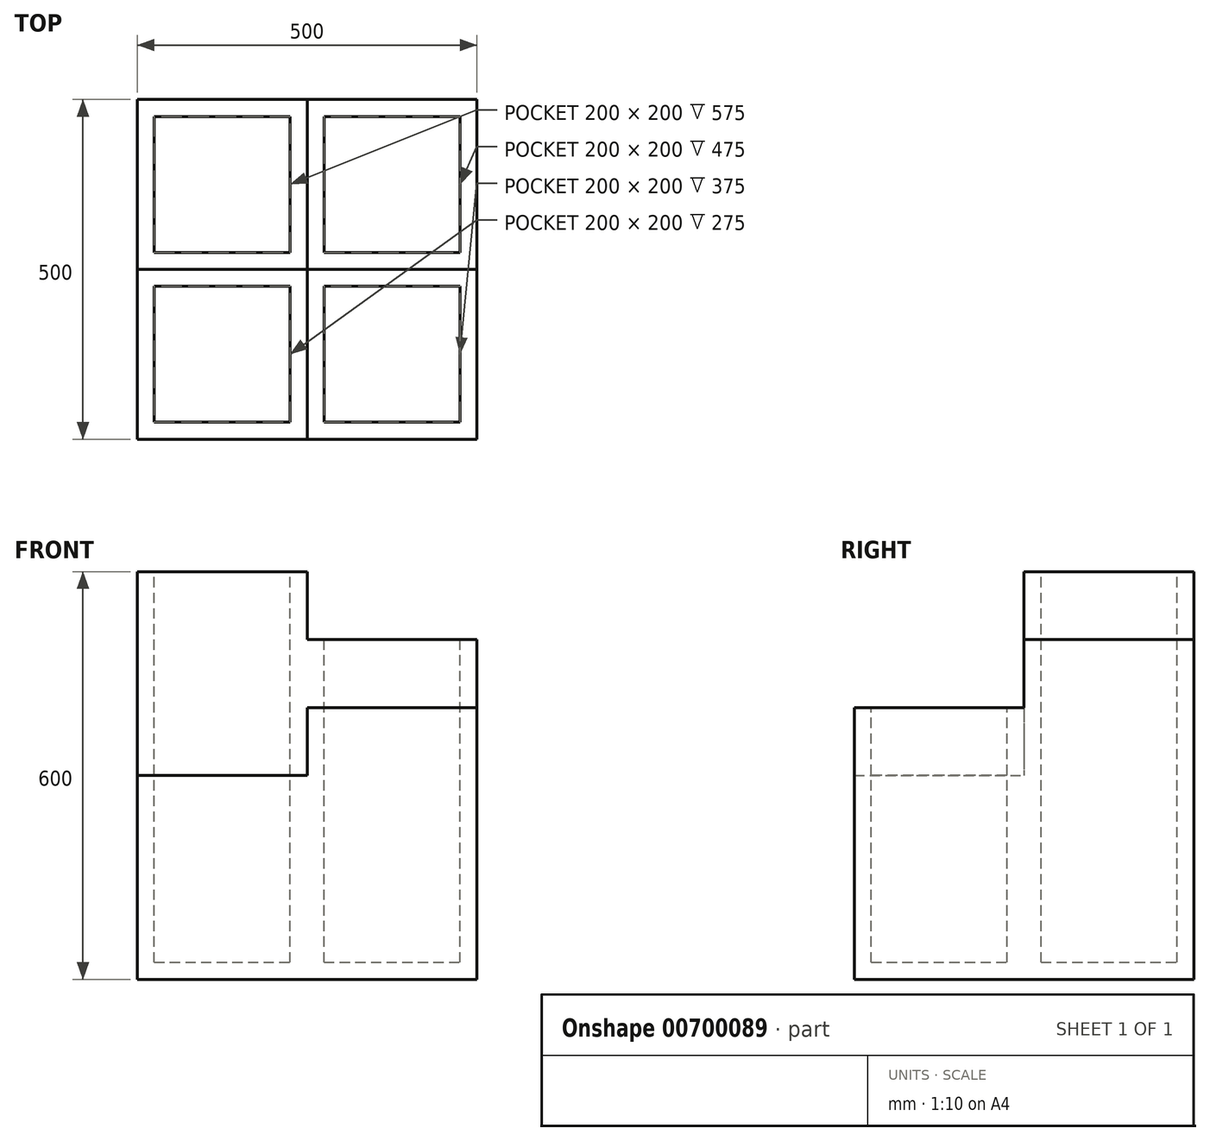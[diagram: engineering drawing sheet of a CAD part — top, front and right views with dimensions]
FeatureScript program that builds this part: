
annotation { "Feature Type Name" : "Feature", "Feature Type Description" : "" }
export const myFeature = defineFeature(function(context is Context, id is Id, definition is map)
    precondition{}
    {
        {
            var Q0;
            Q0=qCreatedBy(makeId("Top.planeOp"),FACE);
            var sketch = newSketch(context, id + "F0", { "sketchPlane" : qUnion([Q0])});
            skLineSegment(sketch, "E0.bottom", {"start": v(0, 0) * mm, "end": v(500, 0) * mm});
            skLineSegment(sketch, "E0.top", {"start": v(0, 500) * mm, "end": v(500, 500) * mm});
            skLineSegment(sketch, "E0.left", {"start": v(0, 0) * mm, "end": v(0, 500) * mm});
            skLineSegment(sketch, "E0.right", {"start": v(500, 0) * mm, "end": v(500, 500) * mm});
            skLineSegment(sketch, "E1", {"start": v(0, 250) * mm, "end": v(500, 250) * mm});
            skLineSegment(sketch, "E2", {"start": v(250, 500) * mm, "end": v(250, 0) * mm});
            skSolve(sketch);
        }
        {
            var Q0;
            {var subQ0=sQuery(id+"F0.wireOp",EDGE,"E0.left");var subQ1=sQuery(id+"F0.wireOp",EDGE,"E0.top");var subQ2=makeQuery(id+"F0.imprint","INTERSECT",VERTEX,{"derivedFrom":[subQ1,subQ0]});Q0=makeQuery(id+"F0.imprint","IMPRINT",FACE,{"disambiguationData":[TD([[makeQuery(id+"F0.imprint","IMPRINT",EDGE,{"disambiguationData":[TD([[subQ2,-1.0]])],"derivedFrom":subQ1}),-1.0]])]});}
            extrude(context, id + "F1", {"entities" : qUnion([Q0]), "depth" : 600 * mm, "offsetDistance" : 25 * mm});
        }
        {
            var Q0;
            {var subQ0=sQuery(id+"F0.wireOp",EDGE,"E0.right");var subQ1=sQuery(id+"F0.wireOp",EDGE,"E0.top");var subQ2=makeQuery(id+"F0.imprint","INTERSECT",VERTEX,{"derivedFrom":[subQ1,subQ0]});Q0=makeQuery(id+"F0.imprint","IMPRINT",FACE,{"disambiguationData":[TD([[makeQuery(id+"F0.imprint","IMPRINT",EDGE,{"disambiguationData":[TD([[subQ2,1.0]])],"derivedFrom":subQ1}),-1.0]])]});}
            extrude(context, id + "F2", {"entities" : qUnion([Q0]), "operationType" : NewBodyOperationType.ADD, "depth" : 500 * mm, "offsetDistance" : 25 * mm});
        }
        {
            var Q0;
            {var subQ0=sQuery(id+"F0.wireOp",EDGE,"E0.right");var subQ1=sQuery(id+"F0.wireOp",EDGE,"E0.bottom");var subQ2=makeQuery(id+"F0.imprint","INTERSECT",VERTEX,{"derivedFrom":[subQ1,subQ0]});Q0=makeQuery(id+"F0.imprint","IMPRINT",FACE,{"disambiguationData":[TD([[makeQuery(id+"F0.imprint","IMPRINT",EDGE,{"disambiguationData":[TD([[subQ2,1.0]])],"derivedFrom":subQ1}),1.0]])]});}
            extrude(context, id + "F3", {"entities" : qUnion([Q0]), "operationType" : NewBodyOperationType.ADD, "depth" : 400 * mm, "offsetDistance" : 25 * mm});
        }
        {
            var Q0;
            {var subQ0=sQuery(id+"F0.wireOp",EDGE,"E0.left");var subQ1=sQuery(id+"F0.wireOp",EDGE,"E0.bottom");var subQ2=makeQuery(id+"F0.imprint","INTERSECT",VERTEX,{"derivedFrom":[subQ1,subQ0]});Q0=makeQuery(id+"F0.imprint","IMPRINT",FACE,{"disambiguationData":[TD([[makeQuery(id+"F0.imprint","IMPRINT",EDGE,{"disambiguationData":[TD([[subQ2,-1.0]])],"derivedFrom":subQ1}),1.0]])]});}
            extrude(context, id + "F4", {"entities" : qUnion([Q0]), "operationType" : NewBodyOperationType.ADD, "depth" : 300 * mm, "offsetDistance" : 25 * mm});
        }
        {
            var Q0;
            Q0=makeQuery(id+"F1.opExtrude","CAP_FACE",FACE,{"disambiguationData":[OSD([sQuery(id+"F0.wireOp",EDGE,"E0.top"),sQuery(id+"F0.wireOp",EDGE,"E0.left"),sQuery(id+"F0.wireOp",EDGE,"E1"),sQuery(id+"F0.wireOp",EDGE,"E2")])],"isStart":false});
            var sketch = newSketch(context, id + "F5", { "sketchPlane" : qUnion([Q0])});
            skLineSegment(sketch, "E3.0", {"start": v(25, 275) * mm, "end": v(225, 275) * mm});
            skLineSegment(sketch, "E3.1", {"start": v(25, 275) * mm, "end": v(25, 475) * mm});
            skLineSegment(sketch, "E3.2", {"start": v(25, 475) * mm, "end": v(225, 475) * mm});
            skLineSegment(sketch, "E3.3", {"start": v(225, 475) * mm, "end": v(225, 275) * mm});
            skSolve(sketch);
        }
        {
            var Q0;
            Q0 = qSketchRegion(id + "F5", true);
            extrude(context, id + "F6", {"entities" : qUnion([Q0]), "operationType" : NewBodyOperationType.REMOVE, "oppositeDirection" : true, "depth" : 575 * mm, "offsetDistance" : 25 * mm});
        }
        {
            var Q0;
            Q0=makeQuery(id+"F2.opExtrude","CAP_FACE",FACE,{"disambiguationData":[OSD([sQuery(id+"F0.wireOp",EDGE,"E0.top"),sQuery(id+"F0.wireOp",EDGE,"E0.right"),sQuery(id+"F0.wireOp",EDGE,"E1"),sQuery(id+"F0.wireOp",EDGE,"E2")])],"isStart":false});
            var sketch = newSketch(context, id + "F7", { "sketchPlane" : qUnion([Q0])});
            skLineSegment(sketch, "E4.0", {"start": v(275, 275) * mm, "end": v(475, 275) * mm});
            skLineSegment(sketch, "E4.1", {"start": v(275, 475) * mm, "end": v(275, 275) * mm});
            skLineSegment(sketch, "E4.2", {"start": v(275, 475) * mm, "end": v(475, 475) * mm});
            skLineSegment(sketch, "E4.3", {"start": v(475, 275) * mm, "end": v(475, 475) * mm});
            skSolve(sketch);
        }
        {
            var Q0;
            Q0 = qSketchRegion(id + "F7", true);
            extrude(context, id + "F8", {"entities" : qUnion([Q0]), "operationType" : NewBodyOperationType.REMOVE, "oppositeDirection" : true, "depth" : 475 * mm, "offsetDistance" : 25 * mm});
        }
        {
            var Q0;
            Q0=makeQuery(id+"F3.opExtrude","CAP_FACE",FACE,{"disambiguationData":[OSD([sQuery(id+"F0.wireOp",EDGE,"E0.bottom"),sQuery(id+"F0.wireOp",EDGE,"E0.right"),sQuery(id+"F0.wireOp",EDGE,"E1"),sQuery(id+"F0.wireOp",EDGE,"E2")])],"isStart":false});
            var sketch = newSketch(context, id + "F9", { "sketchPlane" : qUnion([Q0])});
            skLineSegment(sketch, "E5.0", {"start": v(475, 225) * mm, "end": v(275, 225) * mm});
            skLineSegment(sketch, "E5.1", {"start": v(475, 25) * mm, "end": v(475, 225) * mm});
            skLineSegment(sketch, "E5.2", {"start": v(275, 25) * mm, "end": v(475, 25) * mm});
            skLineSegment(sketch, "E5.3", {"start": v(275, 225) * mm, "end": v(275, 25) * mm});
            skSolve(sketch);
        }
        {
            var Q0;
            Q0 = qSketchRegion(id + "F9", true);
            extrude(context, id + "F10", {"entities" : qUnion([Q0]), "operationType" : NewBodyOperationType.REMOVE, "oppositeDirection" : true, "depth" : 375 * mm, "offsetDistance" : 25 * mm});
        }
        {
            var Q0;
            Q0=makeQuery(id+"F4.opExtrude","CAP_FACE",FACE,{"disambiguationData":[OSD([sQuery(id+"F0.wireOp",EDGE,"E0.bottom"),sQuery(id+"F0.wireOp",EDGE,"E0.left"),sQuery(id+"F0.wireOp",EDGE,"E1"),sQuery(id+"F0.wireOp",EDGE,"E2")])],"isStart":false});
            var sketch = newSketch(context, id + "F11", { "sketchPlane" : qUnion([Q0])});
            skLineSegment(sketch, "E6.0", {"start": v(225, 25) * mm, "end": v(225, 225) * mm});
            skLineSegment(sketch, "E6.1", {"start": v(25, 25) * mm, "end": v(225, 25) * mm});
            skLineSegment(sketch, "E6.2", {"start": v(25, 225) * mm, "end": v(25, 25) * mm});
            skLineSegment(sketch, "E6.3", {"start": v(225, 225) * mm, "end": v(25, 225) * mm});
            skSolve(sketch);
        }
        {
            var Q0;
            Q0 = qSketchRegion(id + "F11", true);
            extrude(context, id + "F12", {"entities" : qUnion([Q0]), "operationType" : NewBodyOperationType.REMOVE, "oppositeDirection" : true, "depth" : 275 * mm, "offsetDistance" : 25 * mm});
        }
    });
